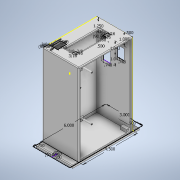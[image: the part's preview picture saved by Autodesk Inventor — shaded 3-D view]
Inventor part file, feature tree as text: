
AUTODESK INVENTOR PART (.ipt)
format: ipt  version: 2020 (Build 240168000, 168)  size: 1,515,008 bytes
history: native  units: in
note: dims shown in document units (in); Inventor stores cm internally (conversion verified against a paired STEP export)
features: sketch x18, extrude x17, hole x5, fillet x3, thread x2, pattern_linear x2, other x1
ambient origin geometry x8: Origin, YZ Plane, XZ Plane, XY Plane, X Axis, Y Axis, Z Axis, Center Point
bodies: Solid1 (feature_tree)
feature tree (48):
  sketch  "Sketch1"  dims[d0=3.0in d1=6.0in]
  extrude  "Extrusion1"  Depth=6.0in
  extrude  "Extrusion2"  Depth=0.75in
  hole  "Hole1"  [1 undecoded]
  extrude  "Extrusion7"  Depth=0.1875in
  extrude  "Extrusion8"  Depth=0.1875in
  extrude  "Extrusion3"  Depth=0.125in
  extrude  "Extrusion4"  Depth=0.125in
  extrude  "Extrusion5"  Depth=0.125in TaperAngle=0.0deg
  extrude  "Extrusion6"  Depth=0.25in
  extrude  "Extrusion9"  Depth=0.5in
  hole  "Hole2"  [1 undecoded]
  thread  "Thread1"  [1 undecoded]
  pattern_linear  "Rectangular Pattern1"  Spacing1=0.25in  [1 undecoded]
  extrude  "Extrusion10"  Depth=0.125in
  sketch  "Sketch13"  dims[d32=0.25in d33=0.25in d34=0.0in d35=0.5906in]
  hole  "Hole5"  [1 undecoded]
  thread  "Thread3"  [1 undecoded]
  pattern_linear  "Rectangular Pattern2"  Count1=2 Spacing1=1.9291in
  hole  "Hole4"  [1 undecoded]
  fillet  "Fillet1"  Radius=0.3937in
  extrude  "Extrusion11"  Depth=0.8406in TaperAngle=0.0deg
  extrude  "Extrusion12"  Depth=0.125in
  sketch  "Sketch18"  dims[d38=2.2835in]
  extrude  "Extrusion13"  Depth=0.1875in
  hole  "Hole6"  [1 undecoded]
  fillet  "Fillet2"  Radius=0.125in
  other  "iFeature13:2"
  sketch  "Sketch20"  dims[d41=0.5in]
  extrude  "Extrusion14"  Depth=0.125in
  extrude  "Extrusion15"  Depth=0.0625in
  sketch  "Sketch21"  dims[d42=90.0deg d43=0.25in d44=0.0in d45=0.1181in d46=0.25in d47=0.0in d48=0.0793in d49=0.197in d50=0.119in d51=0.188in d52=90.0deg d53=0.25in d54=0.8108in d55=0.25in d56=0.0in d57=0.7874in d59=1.9291in d60=0.7874in d62=2.2835in d63=0.3937in d65=0.8406in d66=0.0in d76=0.7874in d78=2.6772in d79=0.7874in d81=3.7008in d82=0.1875in d83=0.1875in d84=0.125in d85=0.125in d86=0.1562in d87=0.197in d88=0.119in d89=0.188in d90=0.5635in d91=0.259in d92=0.8108in d93=0.0625in d94=0.1969in d95=0.1181in d96=0.0793in d97=0.197in d98=0.119in d99=0.188in d100=0.5635in d101=0.259in d102=0.8108in d103=0.841in d104=0.0in d128=2.75in d130=1.5in d131=0.0in d132=1.0in d133=3.0in d134=0.0625in d135=0.0in d136=1.5in d137=0.5in d138=90.0deg d139=0.75in d140=2.75in d141=0.125in d142=0.0in d143=0.375in d144=0.375in d145=0.375in d146=0.375in d147=0.375in d148=0.0in d149=0.1875in d150=0.1875in d151=0.1875in d152=0.1875in d153=0.1562in d154=0.197in d155=0.119in d156=0.188in d157=0.5635in d158=0.259in d159=0.8108in d160=0.0625in d161=0.12in d163=0.492in d165=0.129in d167=0.04in d173=1.25in d174=0.75in d175=90.0deg d176=0.4331in d177=0.375in d178=0.0in d179=0.5in d180=1.0in d181=0.748in d182=1.043in d183=0.5in d184=0.748in d185=1.043in d186=0.0197in d187=0.0in d188=0.375in d189=90.0deg d190=0.25in d191=90.0deg d192=0.5in d193=0.75in d194=0.25in d195=0.0in d196=0.0197in d197=0.0in d198=0.125in]
  extrude  "Extrusion16"  Depth=0.125in
  extrude  "Extrusion17"  Depth=0.125in
  fillet  "Fillet3"  Radius=0.841in
  sketch  "Sketch2"  dims[d2=0.75in d3=4.5in]
  sketch  "Sketch3"  dims[d4=0.1875in d5=0.0in d6=6.75in d7=0.0in]
  sketch  "Sketch4"  dims[d8=0.5in]
  sketch  "Sketch5"  dims[d9=0.266in d10=0.75in d11=0.507in d12=0.0625in d13=0.5635in d14=1.0in d15=0.8108in d16=0.1875in]
  sketch  "Sketch6"  dims[d17=0.1875in d18=0.1875in]
  sketch  "Sketch7"  dims[d19=2.8125in d20=0.0in d21=0.125in]
  sketch  "Sketch8"  dims[d22=0.125in d23=0.125in]
  sketch  "Sketch9"  dims[d24=0.125in d25=0.125in d26=0.0in]
  sketch  "Sketch10"  dims[d27=0.5in d28=0.25in]
  sketch  "Sketch12"  dims[d29=0.25in d30=0.0in d31=0.5in]
  sketch  "Sketch16"  dims[d36=0.3937in]
  sketch  "Sketch17"  dims[d37=1.9291in]
  sketch  "Sketch19"  dims[d39=0.25in d40=0.0in]
note: 8 required parameter values undecoded (feature->parameter linkage not recoverable at this tier; creation-order binding heuristic only, values carry confidence <= 0.55)
